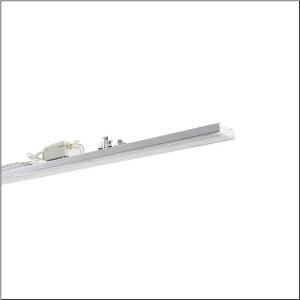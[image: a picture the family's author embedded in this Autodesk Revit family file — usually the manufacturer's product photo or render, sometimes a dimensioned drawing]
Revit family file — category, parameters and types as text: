
# Revit family: licross_r__21_recessed_ho_52tl12cn495m_a1ad
name_source: partatom
category: Lighting Fixtures
units: mm (PartAtom-declared; Revit-internal decimal feet)

## family parameters
Cut with Voids When Loaded = No
Host = Face
Light Source = No
Part Type = Normal
Room Calculation Point = No
Round Connector Dimension = Use Diameter
Shared = No

## types (1)
- --- (1 x LED, 10000 lm, 53 W, 4000K)
    Apparent Load = 53 VA
    CIE Flux Codes = 69 91 98 100 100
    Color Rendering = 80
    Color Temperature = 4000K
    Default Elevation = 1800 mm
    Description = Licross® 21 Recessed HO, luminaire insert, of sheet steel, galvanised, coil coated, white, length: 1.500mm, width: 66mm, height: 67mm, LED rated luminous flux: 9.990lm, light colour: 840, control gear: ON/OFF Multilumen, CLOi, control gear: ECG Multilumen, with plug, 3-pole, with phase selection, mains connection: 220..240V, AC, 50/60Hz, halogen-free wiring, primary optical cover: cover, of PMMA, light emission: direct distribution, primary light characteristic: symmetric, protection rating (complete): IP40, insulation class (complete): insulation class I (protective earthing), certification: CE, ENEC, VDE, UKCA, protection symbol: D if used in an environment without relevant dust loads with corresponding accessories, impact resistance: IK06, permissible ambient temperature for indoor applications: -35..+35°C, corresponds to IFS (International Featured Standards) requirements for safety and quality in the food industry, reducing of maximum allowable ambient temperature of 5°C with ceiling mounting, LABS conformity tested according to VDMA 24364:2018-05, packaging unit: 1 piece
    Height = 58 mm
    Lamp = 1 x LED
    Lamp Light Flux = 10000 lm
    Lamp Power = 53 W
    Lamp count = 1
    Length = 1500 mm
    Luminous efficacy = 189 lm/W
    Manufacturer = Siteco
    ModVariant = No
    Model = 52TL12CN495M
    Mounting Place = Ceiling
    Mounting Type = Pendant
    Number of Poles = 1
    OnlyDefault = Yes
    Power Factor = 1
    Product Name = Licross® 21 Recessed HO
    Product group = luminaire insert
    ProductGroupID = 901
    Protection Class = Protection class I
    Protection Degree = IP 40
    RLX_Detail_Level = 1
    RLX_Emergency_Light_Flux = 0 lm
    RLX_Emergency_Type = 0
    RLX_Emergency_Type_DB = No
    RlxData = <blob elided: 22321 chars, md5=8a6f1343>
    Socket = socket
    Standby Power = 0 W
    System Light Flux = 10000 lm
    System Power = 53 W
    Type Comments = factory setting: luminous flux: 100 % | (A | C | E) | 125 mA
    Type Image = l_1296930.jpg
    URL = http://relux.com
    VarID = @adj_078705
    Voltage = 0 V
    Weight = 0.00 kg
    Width = 66 mm

## geometry (parser evidence)
native form markers: Blend x4, Sweep x9
no freeform markers — native parametric forms only
